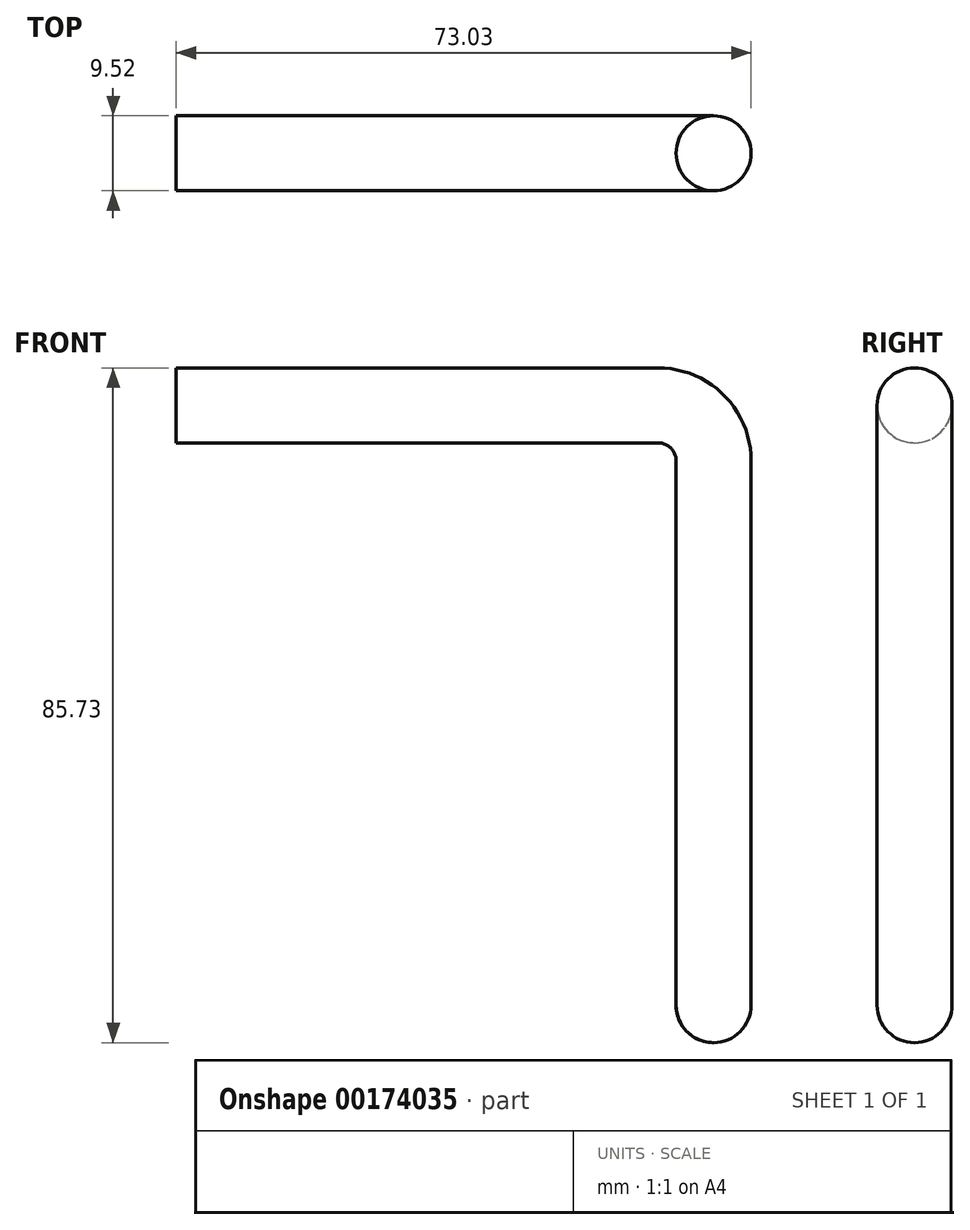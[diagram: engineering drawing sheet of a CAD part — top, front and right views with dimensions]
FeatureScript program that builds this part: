
annotation { "Feature Type Name" : "Feature", "Feature Type Description" : "" }
export const myFeature = defineFeature(function(context is Context, id is Id, definition is map)
    precondition{}
    {
        {
            var Q0;
            Q0=qCreatedBy(makeId("Front.planeOp"),FACE);
            var sketch = newSketch(context, id + "F0", { "sketchPlane" : qUnion([Q0])});
            skLineSegment(sketch, "E0", {"start": v(0, 0) * mm, "end": v(61.21, 0) * mm, "construction": true});
            skLineSegment(sketch, "E1", {"start": v(63.5, -2.29) * mm, "end": v(63.5, -76.2) * mm, "construction": true});
            skArc(sketch, "E2", {"start": v(63.5, -2.29) * mm, "mid": v(62.83, -0.67) * mm, "end": v(61.21, 0) * mm, "construction": true});
            skLineSegment(sketch, "E3.0", {"start": v(68.26, -2.29) * mm, "end": v(68.26, -76.2) * mm});
            skArc(sketch, "E3.1", {"start": v(68.26, -2.29) * mm, "mid": v(66.2, 2.7) * mm, "end": v(61.21, 4.76) * mm});
            skLineSegment(sketch, "E3.2", {"start": v(0, 4.76) * mm, "end": v(61.21, 4.76) * mm});
            skSolve(sketch);
        }
        {
            var Q0;
            Q0=qCreatedBy(makeId("Right.planeOp"),FACE);
            var sketch = newSketch(context, id + "F1", { "sketchPlane" : qUnion([Q0])});
            skCircle(sketch, "E4", {"center": v(0, 4.76) * mm, "radius": 4.76 * mm});
            skSolve(sketch);
        }
        {
            var Q0;
            Q0=makeQuery(id+"F1.imprint","IMPRINT",FACE,{"disambiguationData":[TD([[makeQuery(id+"F1.imprint","IMPRINT",EDGE,{"derivedFrom":sQuery(id+"F1.wireOp",EDGE,"E4")}),1.0]])]});
            var Q1;
            Q1=sQuery(id+"F0.wireOp",EDGE,"E3.2");
            var Q2;
            Q2=sQuery(id+"F0.wireOp",EDGE,"E3.1");
            var Q3;
            Q3=sQuery(id+"F0.wireOp",EDGE,"E3.0");
            sweep(context, id + "F2", {"profiles" : qUnion([Q0]), "path" : qUnion([Q1, Q2, Q3])});
        }
        {
            var Q0;
            Q0=makeQuery(id+"F2.opSweep","CAP_EDGE",EDGE,{"disambiguationData":[OSD([sQuery(id+"F0.wireOp",VERTEX,"E3.0.end"),sQuery(id+"F1.wireOp",EDGE,"E4")])],"isStart":false});
            fillet(context, id + "F3", {"entities" : qUnion([Q0]), "radius" : 4.76 * mm, "tangentPropagation" : true, "allowEdgeOverflow" : false});
        }
    });
